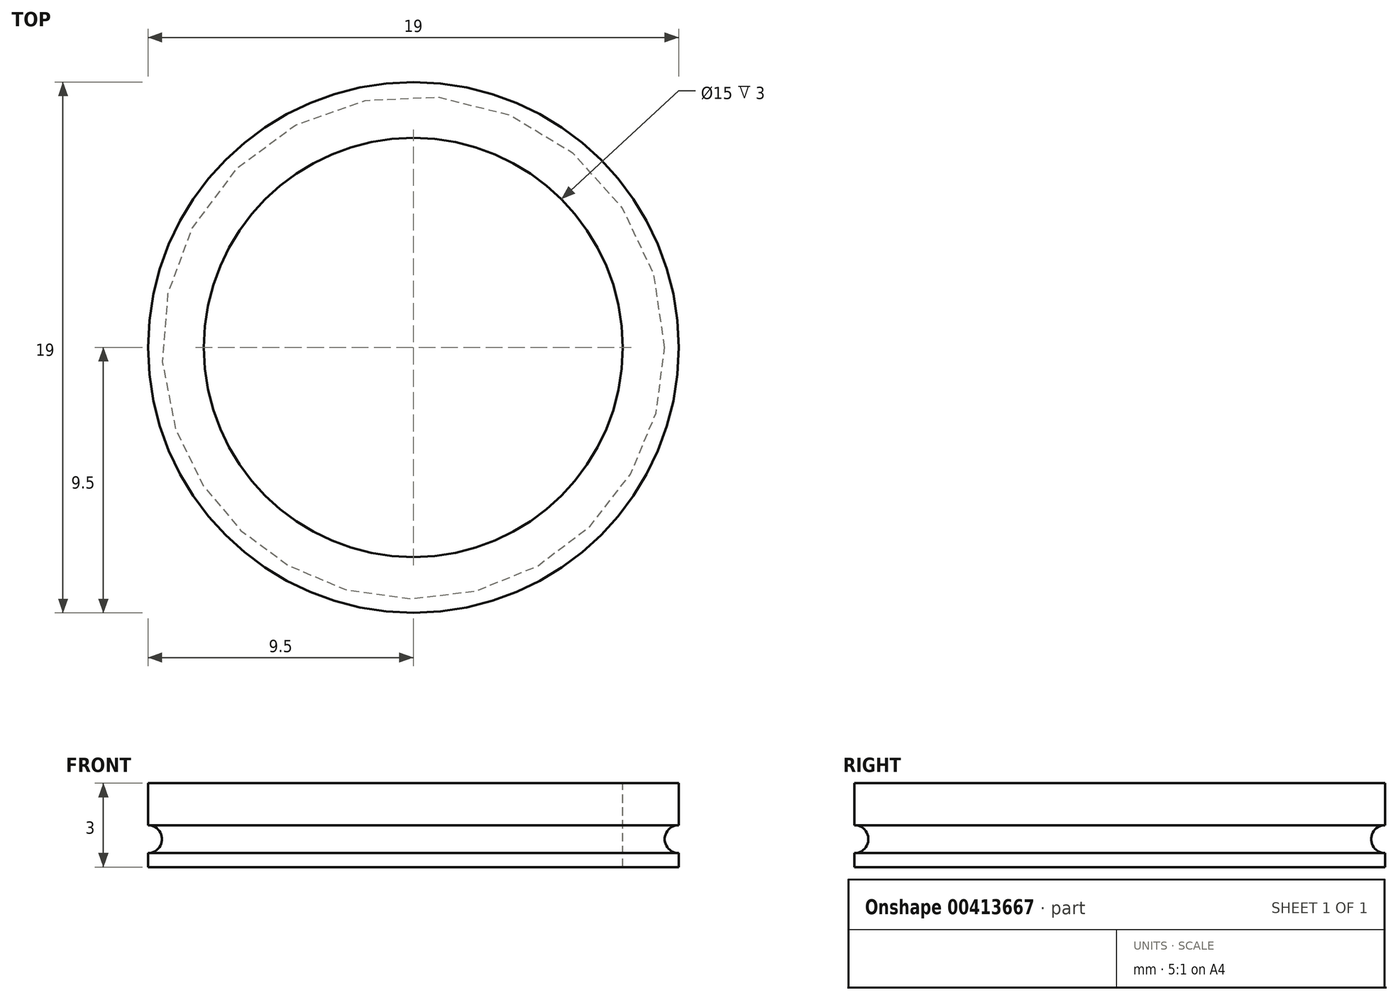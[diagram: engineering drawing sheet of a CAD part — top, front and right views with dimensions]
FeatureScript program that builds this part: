
annotation { "Feature Type Name" : "Feature", "Feature Type Description" : "" }
export const myFeature = defineFeature(function(context is Context, id is Id, definition is map)
    precondition{}
    {
        {
            var Q0;
            Q0=qCreatedBy(makeId("Top.planeOp"),FACE);
            var sketch = newSketch(context, id + "F0", { "sketchPlane" : qUnion([Q0])});
            skCircle(sketch, "E0", {"center": v(0, 0) * mm, "radius": 9.5 * mm});
            skSolve(sketch);
        }
        {
            var Q0;
            Q0 = qSketchRegion(id + "F0", true);
            var Q1;
            Q1=sQuery(id+"F0.wireOp",EDGE,"E0");
            extrude(context, id + "F1", {"entities" : qUnion([Q0]), "surfaceEntities" : qUnion([Q1]), "depth" : 3 * mm, "offsetDistance" : 25 * mm});
        }
        {
            var Q0;
            Q0=qCreatedBy(makeId("Front.planeOp"),FACE);
            var sketch = newSketch(context, id + "F2", { "sketchPlane" : qUnion([Q0])});
            skCircle(sketch, "E1", {"center": v(9.5, 1) * mm, "radius": 0.5 * mm});
            skSolve(sketch);
        }
        {
            var Q0;
            Q0=qCreatedBy(makeId("Top.planeOp"),FACE);
            cPlane(context, id + "F3", {"entities" : qUnion([Q0]), "cplaneType" : CPlaneType.OFFSET, "offset" : 1 * mm, "width" : 150 * mm, "height" : 150 * mm});
        }
        {
            var Q0;
            Q0=qCreatedBy(id+"F3.planeOp",FACE);
            var sketch = newSketch(context, id + "F4", { "sketchPlane" : qUnion([Q0])});
            skCircle(sketch, "E2", {"center": v(0, 0) * mm, "radius": 9.5 * mm});
            skSolve(sketch);
        }
        {
            var Q0;
            Q0 = qSketchRegion(id + "F2", true);
            var Q1;
            Q1 = qConstructionFilter(qBodyType(qCreatedBy(id + "F4" ,EDGE), BodyType.WIRE), ConstructionObject.NO);
            sweep(context, id + "F5", {"operationType" : NewBodyOperationType.REMOVE, "profiles" : qUnion([Q0]), "path" : qUnion([Q1])});
        }
        {
            var Q0;
            Q0=makeQuery(id+"F1.opExtrude","CAP_FACE",FACE,{"disambiguationData":[OSD([sQuery(id+"F0.wireOp",EDGE,"E0")])],"isStart":true});
            var sketch = newSketch(context, id + "F6", { "sketchPlane" : qUnion([Q0])});
            skPoint(sketch, "E3", {"position": v(0, 0) * mm});
            skSolve(sketch);
        }
        {
            var Q0;
            Q0=sQuery(id+"F6.wireOp",VERTEX,"E3");
            var Q1;
            Q1=makeQuery(id+"F1.opExtrude","SWEPT_BODY",BODY,{"disambiguationData":[OSD([sQuery(id+"F0.wireOp",EDGE,"E0")])]});
            hole(context, id + "F7", {"style" : HoleStyle.SIMPLE, "endStyle" : HoleEndStyle.THROUGH, "holeDiameter" : 15 * mm, "majorDiameter" : 5 * mm, "isTappedThrough" : true, "tappedDepth" : 12 * mm, "tapClearance" : 3, "locations" : qUnion([Q0]), "scope" : qUnion([Q1]), "startStyle" : HoleStartStyle.SKETCH});
        }
    });
